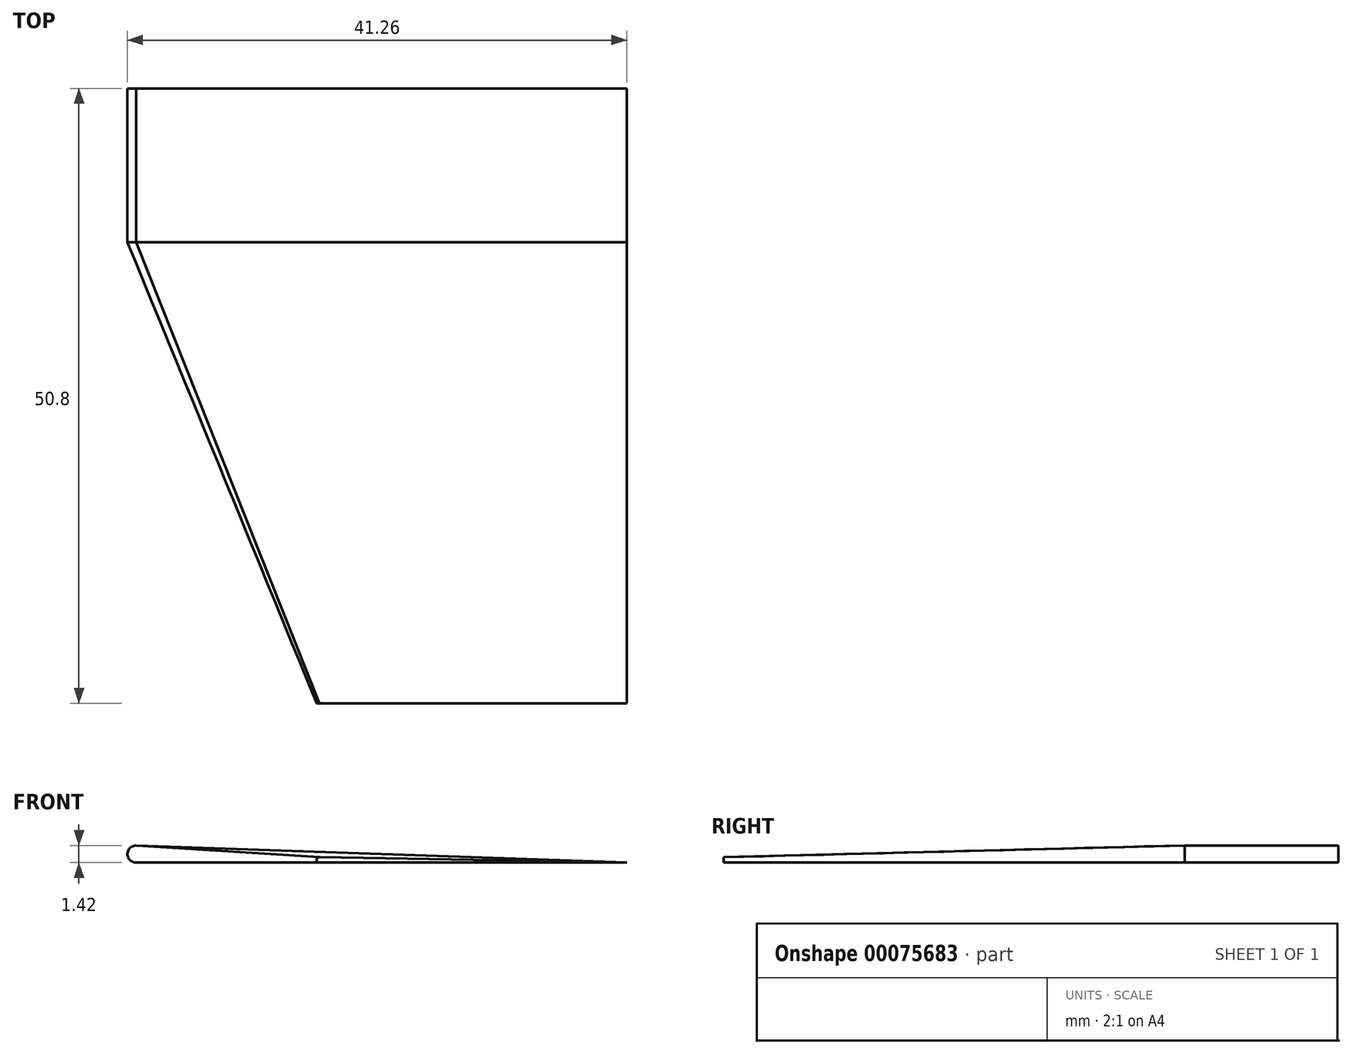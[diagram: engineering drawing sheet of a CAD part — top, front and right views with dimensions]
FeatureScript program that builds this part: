
annotation { "Feature Type Name" : "Feature", "Feature Type Description" : "" }
export const myFeature = defineFeature(function(context is Context, id is Id, definition is map)
    precondition{}
    {
        {
            var Q0;
            Q0=qCreatedBy(makeId("Front.planeOp"),FACE);
            var sketch = newSketch(context, id + "F0", { "sketchPlane" : qUnion([Q0])});
            skLineSegment(sketch, "E0", {"start": v(0, 0) * mm, "end": v(-40.55, 0) * mm});
            skLineSegment(sketch, "E1", {"start": v(0, 0) * mm, "end": v(-40.55, 1.42) * mm});
            skArc(sketch, "E2", {"start": v(-40.55, 1.42) * mm, "mid": v(-41.26, 0.7) * mm, "end": v(-40.55, 0) * mm});
            skSolve(sketch);
        }
        {
            var Q0;
            Q0=qCreatedBy(makeId("Front.planeOp"),FACE);
            cPlane(context, id + "F1", {"entities" : qUnion([Q0]), "cplaneType" : CPlaneType.OFFSET, "offset" : 50.8 * mm, "width" : 152.4 * mm, "height" : 152.4 * mm});
        }
        {
            var Q0;
            Q0=makeQuery(id+"F0.imprint","IMPRINT",FACE,{"disambiguationData":[TD([[makeQuery(id+"F0.imprint","IMPRINT",EDGE,{"derivedFrom":sQuery(id+"F0.wireOp",EDGE,"E0")}),-1.0]])]});
            extrude(context, id + "F2", {"entities" : qUnion([Q0]), "depth" : 12.7 * mm});
        }
        {
            var Q0;
            Q0=qCreatedBy(id+"F1.planeOp",FACE);
            var sketch = newSketch(context, id + "F3", { "sketchPlane" : qUnion([Q0])});
            skLineSegment(sketch, "E3", {"start": v(0, 0) * mm, "end": v(-25.4, 0) * mm});
            skLineSegment(sketch, "E4", {"start": v(0, 0) * mm, "end": v(-25.4, 0.44) * mm});
            skArc(sketch, "E5", {"start": v(-25.4, 0.44) * mm, "mid": v(-25.63, 0.22) * mm, "end": v(-25.4, 0) * mm});
            skSolve(sketch);
        }
        {
            var Q1;
            Q1=makeQuery(id+"F2.opExtrude","CAP_FACE",FACE,{"disambiguationData":[OSD([sQuery(id+"F0.wireOp",EDGE,"E0"),sQuery(id+"F0.wireOp",EDGE,"E1"),sQuery(id+"F0.wireOp",EDGE,"E2")])],"isStart":false});
            var Q2;
            Q2=makeQuery(id+"F3.imprint","IMPRINT",FACE,{"disambiguationData":[TD([[makeQuery(id+"F3.imprint","IMPRINT",EDGE,{"derivedFrom":sQuery(id+"F3.wireOp",EDGE,"E3")}),-1.0]])]});
            loft(context, id + "F4", {"operationType" : NewBodyOperationType.ADD, "sheetProfilesArray" : [{ "sheetProfileEntities" : qUnion([Q1]) }, { "sheetProfileEntities" : qUnion([Q2]) }]});
        }
    });
